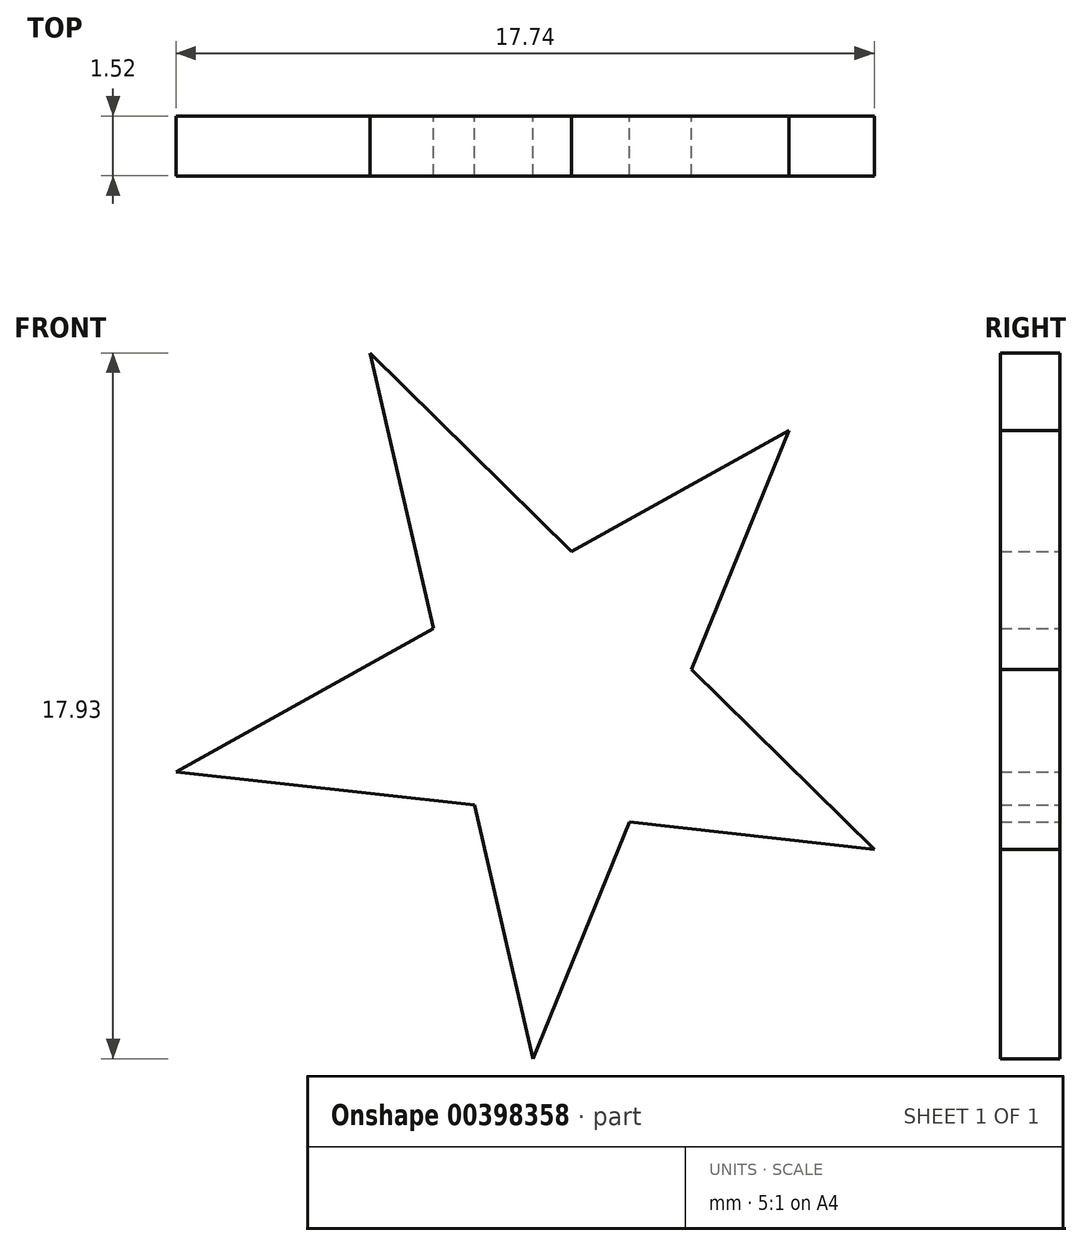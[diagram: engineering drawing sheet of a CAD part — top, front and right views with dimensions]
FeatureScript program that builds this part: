
annotation { "Feature Type Name" : "Feature", "Feature Type Description" : "" }
export const myFeature = defineFeature(function(context is Context, id is Id, definition is map)
    precondition{}
    {
        {
            var Q0;
            Q0=qCreatedBy(makeId("Front.planeOp"),FACE);
            var sketch = newSketch(context, id + "F0", { "sketchPlane" : qUnion([Q0])});
            skLineSegment(sketch, "E0", {"start": v(-18.15, -40.2) * mm, "end": v(-19.64, -33.75) * mm});
            skLineSegment(sketch, "E1", {"start": v(-22.3, -22.27) * mm, "end": v(-17.17, -27.31) * mm});
            skLineSegment(sketch, "E2", {"start": v(-9.48, -34.88) * mm, "end": v(-15.7, -34.19) * mm});
            skLineSegment(sketch, "E3", {"start": v(-27.22, -32.91) * mm, "end": v(-20.68, -29.27) * mm});
            skLineSegment(sketch, "E4", {"start": v(-11.65, -24.24) * mm, "end": v(-14.12, -30.31) * mm});
            skLineSegment(sketch, "E5.trimOffspring", {"start": v(-20.68, -29.27) * mm, "end": v(-22.3, -22.27) * mm});
            skLineSegment(sketch, "E6.trimOffspring", {"start": v(-14.12, -30.31) * mm, "end": v(-9.48, -34.88) * mm});
            skLineSegment(sketch, "E7.trimOffspring", {"start": v(-17.17, -27.31) * mm, "end": v(-11.65, -24.24) * mm});
            skLineSegment(sketch, "E8.trimOffspring", {"start": v(-15.7, -34.19) * mm, "end": v(-18.15, -40.2) * mm});
            skLineSegment(sketch, "E9.trimOffspring", {"start": v(-19.64, -33.75) * mm, "end": v(-27.22, -32.91) * mm});
            skSolve(sketch);
        }
        {
            var Q0;
            Q0=makeQuery(id+"F0.imprint","IMPRINT",FACE,{"disambiguationData":[TD([[makeQuery(id+"F0.imprint","IMPRINT",EDGE,{"derivedFrom":sQuery(id+"F0.wireOp",EDGE,"E0")}),-1.0]])]});
            extrude(context, id + "F1", {"entities" : qUnion([Q0]), "depth" : 1.52 * mm});
        }
    });
